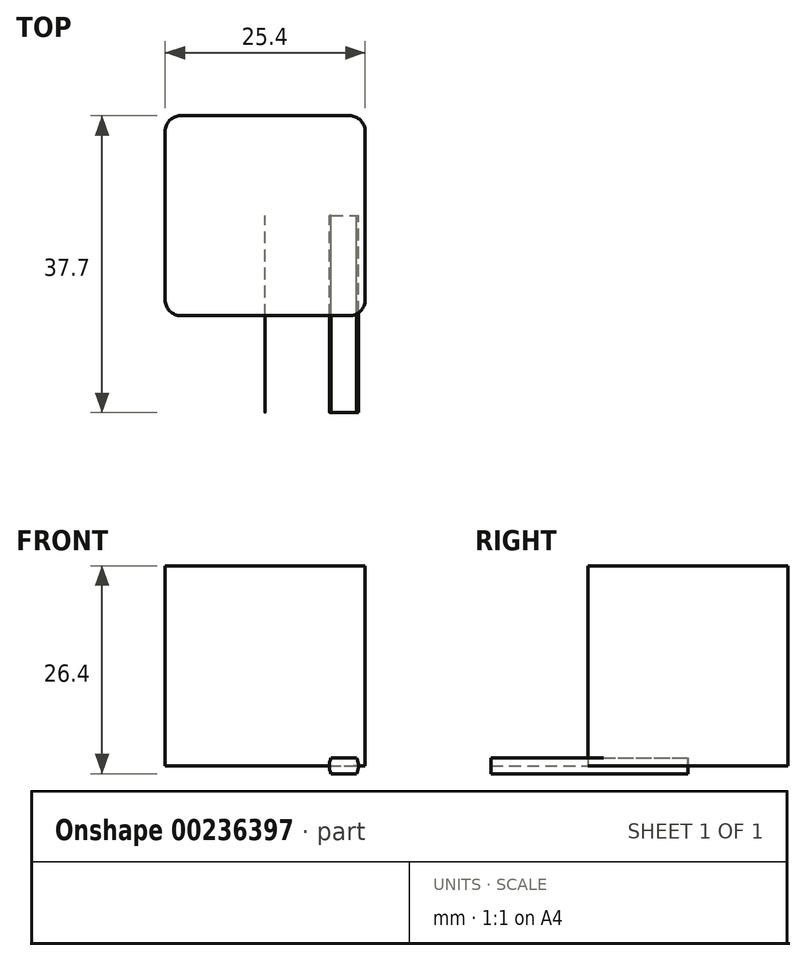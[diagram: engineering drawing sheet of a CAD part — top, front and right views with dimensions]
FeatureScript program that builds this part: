
annotation { "Feature Type Name" : "Feature", "Feature Type Description" : "" }
export const myFeature = defineFeature(function(context is Context, id is Id, definition is map)
    precondition{}
    {
        {
            var Q0;
            Q0=qCreatedBy(makeId("Top.planeOp"),FACE);
            var sketch = newSketch(context, id + "F0", { "sketchPlane" : qUnion([Q0])});
            skLineSegment(sketch, "E0.bottom", {"start": v(-12.7, 12.7) * mm, "end": v(12.7, 12.7) * mm});
            skLineSegment(sketch, "E0.top", {"start": v(-12.7, -12.7) * mm, "end": v(12.7, -12.7) * mm});
            skLineSegment(sketch, "E0.left", {"start": v(-12.7, 12.7) * mm, "end": v(-12.7, -12.7) * mm});
            skLineSegment(sketch, "E0.right", {"start": v(12.7, 12.7) * mm, "end": v(12.7, -12.7) * mm});
            skPoint(sketch, "E0.middle", {"position": v(0, 0) * mm});
            skSolve(sketch);
        }
        {
            var Q0;
            Q0 = qSketchRegion(id + "F0", true);
            extrude(context, id + "F1", {"entities" : qUnion([Q0]), "depth" : 25.4 * mm});
        }
        {
            var Q0;
            Q0=makeQuery(id+"F1.opExtrude","SWEPT_EDGE",EDGE,{"disambiguationData":[OSD([sQuery(id+"F0.wireOp",EDGE,"E0.top"),sQuery(id+"F0.wireOp",EDGE,"E0.left")])]});
            var Q1;
            Q1=makeQuery(id+"F1.opExtrude","SWEPT_EDGE",EDGE,{"disambiguationData":[OSD([sQuery(id+"F0.wireOp",EDGE,"E0.top"),sQuery(id+"F0.wireOp",EDGE,"E0.right")])]});
            var Q2;
            Q2=makeQuery(id+"F1.opExtrude","SWEPT_EDGE",EDGE,{"disambiguationData":[OSD([sQuery(id+"F0.wireOp",EDGE,"E0.bottom"),sQuery(id+"F0.wireOp",EDGE,"E0.left")])]});
            var Q3;
            Q3=makeQuery(id+"F1.opExtrude","SWEPT_EDGE",EDGE,{"disambiguationData":[OSD([sQuery(id+"F0.wireOp",EDGE,"E0.bottom"),sQuery(id+"F0.wireOp",EDGE,"E0.right")])]});
            fillet(context, id + "F2", {"entities" : qUnion([Q0, Q1, Q2, Q3]), "radius" : 2 * mm, "tangentPropagation" : true, "allowEdgeOverflow" : false});
        }
        {
            var Q0;
            Q0=qCreatedBy(makeId("Front.planeOp"),FACE);
            var sketch = newSketch(context, id + "F3", { "sketchPlane" : qUnion([Q0])});
            skCircle(sketch, "E1", {"center": v(0, 0) * mm, "radius": 0.02 * mm});
            skSolve(sketch);
        }
        {
            var Q0;
            Q0 = qSketchRegion(id + "F3", true);
            extrude(context, id + "F4", {"entities" : qUnion([Q0]), "depth" : 25 * mm});
        }
        {
            var Q0;
            Q0=qCreatedBy(makeId("Front.planeOp"),FACE);
            var sketch = newSketch(context, id + "F5", { "sketchPlane" : qUnion([Q0])});
            skLineSegment(sketch, "E2.bottom", {"start": v(8.15, 1) * mm, "end": v(11.85, 1) * mm});
            skLineSegment(sketch, "E2.top", {"start": v(8.15, -1) * mm, "end": v(11.85, -1) * mm});
            skLineSegment(sketch, "E2.left", {"start": v(8.15, 1) * mm, "end": v(8.15, -1) * mm});
            skLineSegment(sketch, "E2.right", {"start": v(11.85, 1) * mm, "end": v(11.85, -1) * mm});
            skPoint(sketch, "E2.middle", {"position": v(10, 0) * mm});
            skArc(sketch, "E3", {"start": v(8.39, 1) * mm, "mid": v(8.15, 0) * mm, "end": v(8.39, -1) * mm});
            skArc(sketch, "E4", {"start": v(11.61, -1) * mm, "mid": v(11.85, 0) * mm, "end": v(11.61, 1) * mm});
            skCircle(sketch, "E5", {"center": v(0, 0) * mm, "radius": 1.5 * mm});
            skSolve(sketch);
        }
        {
            var Q0;
            {var subQ0=sQuery(id+"F5.wireOp",EDGE,"E3");var subQ4=sQuery(id+"F5.wireOp",EDGE,"E2.bottom");var subQ5=makeQuery(id+"F5.imprint","INTERSECT",VERTEX,{"derivedFrom":[subQ4,subQ0]});Q0=makeQuery(id+"F5.imprint","IMPRINT",FACE,{"disambiguationData":[TD([[makeQuery(id+"F5.imprint","IMPRINT",EDGE,{"disambiguationData":[TD([[subQ5,-1.0]])],"derivedFrom":subQ4}),-1.0]])]});}
            extrude(context, id + "F6", {"entities" : qUnion([Q0]), "depth" : 25 * mm});
        }
    });
